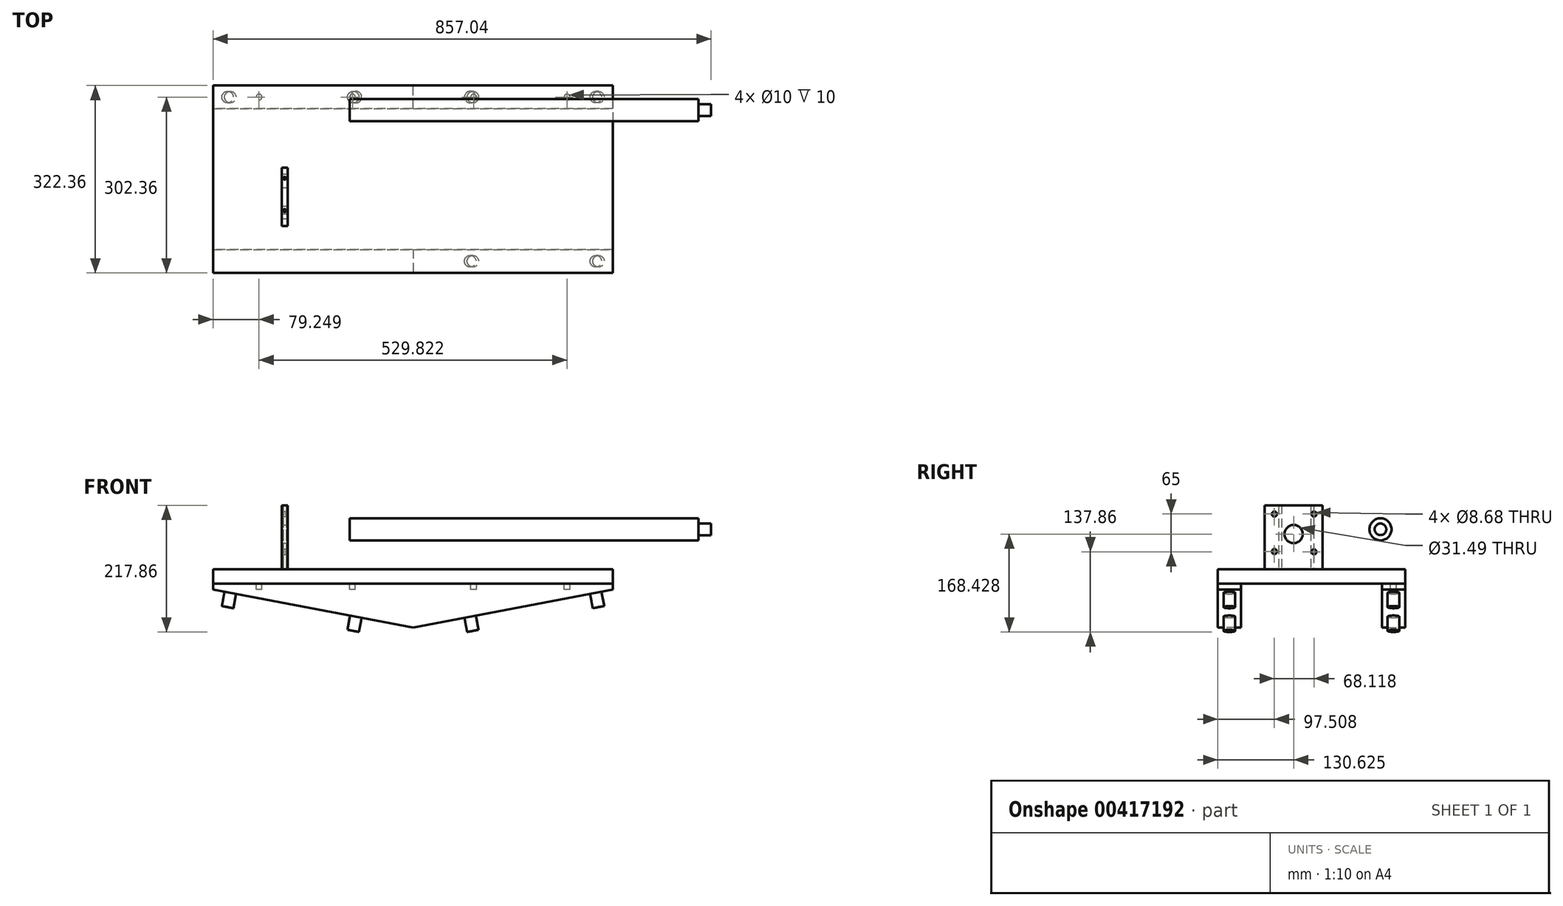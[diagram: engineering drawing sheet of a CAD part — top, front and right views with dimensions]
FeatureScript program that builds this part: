
annotation { "Feature Type Name" : "Feature", "Feature Type Description" : "" }
export const myFeature = defineFeature(function(context is Context, id is Id, definition is map)
    precondition{}
    {
        {
            var Q0;
            Q0=qCreatedBy(makeId("Front.planeOp"),FACE);
            var sketch = newSketch(context, id + "F0", { "sketchPlane" : qUnion([Q0])});
            skLineSegment(sketch, "E0", {"start": v(-343.91, 0) * mm, "end": v(-343.91, -10) * mm});
            skLineSegment(sketch, "E1", {"start": v(-343.91, -10) * mm, "end": v(0, -75) * mm});
            skLineSegment(sketch, "E2", {"start": v(0, -75) * mm, "end": v(343.91, -10) * mm});
            skLineSegment(sketch, "E3", {"start": v(343.91, -10) * mm, "end": v(343.91, 0) * mm});
            skLineSegment(sketch, "E4", {"start": v(343.91, 0) * mm, "end": v(-343.91, 0) * mm});
            skSolve(sketch);
        }
        {
            var Q0;
            Q0 = qSketchRegion(id + "F0", true);
            extrude(context, id + "F1", {"entities" : qUnion([Q0]), "depth" : 40 * mm});
        }
        {
            var Q0;
            Q0=makeQuery(id+"F1.opExtrude","SWEPT_FACE",FACE,{"disambiguationData":[OSD([sQuery(id+"F0.wireOp",EDGE,"E4")])]});
            var sketch = newSketch(context, id + "F2", { "sketchPlane" : qUnion([Q0])});
            skCircle(sketch, "E5", {"center": v(-264.91, -20) * mm, "radius": 5 * mm});
            skCircle(sketch, "E6", {"center": v(-104.19, -20) * mm, "radius": 5 * mm});
            skCircle(sketch, "E7", {"center": v(104.19, -20) * mm, "radius": 5 * mm});
            skCircle(sketch, "E8", {"center": v(264.91, -20) * mm, "radius": 5 * mm});
            skSolve(sketch);
        }
        {
            var Q0;
            Q0 = qSketchRegion(id + "F2", true);
            extrude(context, id + "F3", {"entities" : qUnion([Q0]), "operationType" : NewBodyOperationType.REMOVE, "oppositeDirection" : true, "depth" : 10 * mm});
        }
        {
            var Q0;
            Q0=makeQuery(id+"F1.opExtrude","SWEPT_FACE",FACE,{"disambiguationData":[OSD([sQuery(id+"F0.wireOp",EDGE,"E1")])]});
            var sketch = newSketch(context, id + "F4", { "sketchPlane" : qUnion([Q0])});
            skLineSegment(sketch, "E9", {"start": v(-336.07, 20) * mm, "end": v(13.93, 20) * mm, "construction": true});
            skCircle(sketch, "E10", {"center": v(-306.07, 20) * mm, "radius": 10 * mm});
            skCircle(sketch, "E11", {"center": v(-86.07, 20) * mm, "radius": 10 * mm});
            skSolve(sketch);
        }
        {
            var Q0;
            Q0 = qSketchRegion(id + "F4", true);
            extrude(context, id + "F5", {"entities" : qUnion([Q0]), "operationType" : NewBodyOperationType.ADD, "depth" : 25 * mm});
        }
        {
            var Q0;
            Q0=makeQuery(id+"F1.opExtrude","SWEPT_FACE",FACE,{"disambiguationData":[OSD([sQuery(id+"F0.wireOp",EDGE,"E2")])]});
            var sketch = newSketch(context, id + "F6", { "sketchPlane" : qUnion([Q0])});
            skCircle(sketch, "E12", {"center": v(306.07, 20) * mm, "radius": 10 * mm});
            skLineSegment(sketch, "E13", {"start": v(-13.93, 20) * mm, "end": v(336.07, 20) * mm, "construction": true});
            skCircle(sketch, "E14", {"center": v(86.07, 20) * mm, "radius": 10 * mm});
            skSolve(sketch);
        }
        {
            var Q0;
            Q0 = qSketchRegion(id + "F6", true);
            extrude(context, id + "F7", {"entities" : qUnion([Q0]), "operationType" : NewBodyOperationType.ADD, "depth" : 25 * mm});
        }
        {
            var Q0;
            Q0=qCreatedBy(makeId("Top.planeOp"),FACE);
            var sketch = newSketch(context, id + "F8", { "sketchPlane" : qUnion([Q0])});
            skLineSegment(sketch, "E15.bottom", {"start": v(343.76, 0) * mm, "end": v(-344.16, 0) * mm});
            skLineSegment(sketch, "E15.top", {"start": v(343.76, -322.36) * mm, "end": v(-344.16, -322.36) * mm});
            skLineSegment(sketch, "E15.left", {"start": v(343.76, 0) * mm, "end": v(343.76, -322.36) * mm});
            skLineSegment(sketch, "E15.right", {"start": v(-344.16, 0) * mm, "end": v(-344.16, -322.36) * mm});
            skSolve(sketch);
        }
        {
            var Q0;
            Q0 = qSketchRegion(id + "F8", true);
            extrude(context, id + "F9", {"entities" : qUnion([Q0]), "depth" : 25 * mm});
        }
        {
            var Q0;
            Q0=makeQuery(id+"F9.opExtrude","SWEPT_FACE",FACE,{"disambiguationData":[OSD([sQuery(id+"F8.wireOp",EDGE,"E15.top")])]});
            var sketch = newSketch(context, id + "F10", { "sketchPlane" : qUnion([Q0])});
            skLineSegment(sketch, "E16", {"start": v(-343.91, 0) * mm, "end": v(-343.91, -10) * mm});
            skLineSegment(sketch, "E17", {"start": v(-343.91, -10) * mm, "end": v(0, -75) * mm});
            skLineSegment(sketch, "E18", {"start": v(0, -75) * mm, "end": v(344.01, -10) * mm});
            skLineSegment(sketch, "E19", {"start": v(344.01, -10) * mm, "end": v(344.01, 0) * mm});
            skLineSegment(sketch, "E20", {"start": v(344.01, 0) * mm, "end": v(-343.91, 0) * mm});
            skSolve(sketch);
        }
        {
            var Q0;
            Q0 = qSketchRegion(id + "F10", true);
            extrude(context, id + "F11", {"entities" : qUnion([Q0]), "oppositeDirection" : true, "depth" : 40 * mm});
        }
        {
            var Q0;
            Q0=makeQuery(id+"F11.opExtrude","SWEPT_FACE",FACE,{"disambiguationData":[OSD([sQuery(id+"F10.wireOp",EDGE,"E18")])]});
            var sketch = newSketch(context, id + "F12", { "sketchPlane" : qUnion([Q0])});
            skCircle(sketch, "E21", {"center": v(306.08, 302.36) * mm, "radius": 10 * mm});
            skLineSegment(sketch, "E22", {"start": v(-13.92, 302.36) * mm, "end": v(336.08, 302.36) * mm, "construction": true});
            skCircle(sketch, "E23", {"center": v(86.08, 302.36) * mm, "radius": 10 * mm});
            skSolve(sketch);
        }
        {
            var Q0;
            Q0 = qSketchRegion(id + "F12", true);
            extrude(context, id + "F13", {"entities" : qUnion([Q0]), "operationType" : NewBodyOperationType.ADD, "depth" : 25 * mm});
        }
        {
            var Q0;
            Q0=makeQuery(id+"F9.opExtrude","CAP_FACE",FACE,{"disambiguationData":[OSD([sQuery(id+"F8.wireOp",EDGE,"E15.bottom"),sQuery(id+"F8.wireOp",EDGE,"E15.top"),sQuery(id+"F8.wireOp",EDGE,"E15.left"),sQuery(id+"F8.wireOp",EDGE,"E15.right")])],"isStart":false});
            var sketch = newSketch(context, id + "F14", { "sketchPlane" : qUnion([Q0])});
            skLineSegment(sketch, "E24.bottom", {"start": v(-225.82, -141.73) * mm, "end": v(-215.82, -141.73) * mm});
            skLineSegment(sketch, "E24.top", {"start": v(-225.82, -241.73) * mm, "end": v(-215.82, -241.73) * mm});
            skLineSegment(sketch, "E24.left", {"start": v(-225.82, -141.73) * mm, "end": v(-225.82, -241.73) * mm});
            skLineSegment(sketch, "E24.right", {"start": v(-215.82, -141.73) * mm, "end": v(-215.82, -241.73) * mm});
            skCircle(sketch, "E25", {"center": v(-220.82, -215.24) * mm, "radius": 2.5 * mm});
            skCircle(sketch, "E26", {"center": v(-220.82, -159.56) * mm, "radius": 2.5 * mm});
            skLineSegment(sketch, "E27", {"start": v(-220.82, -141.73) * mm, "end": v(-220.82, -241.73) * mm, "construction": true});
            skSolve(sketch);
        }
        {
            var Q0;
            Q0 = qSketchRegion(id + "F14", true);
            extrude(context, id + "F15", {"entities" : qUnion([Q0]), "depth" : 110 * mm});
        }
        {
            var Q0;
            Q0=makeQuery(id+"F15.opExtrude","SWEPT_FACE",FACE,{"disambiguationData":[OSD([sQuery(id+"F14.wireOp",EDGE,"E24.right")])]});
            var sketch = newSketch(context, id + "F16", { "sketchPlane" : qUnion([Q0])});
            skCircle(sketch, "E28", {"center": v(-156.73, 120) * mm, "radius": 4.34 * mm});
            skCircle(sketch, "E29", {"center": v(-156.73, 55) * mm, "radius": 4.34 * mm});
            skCircle(sketch, "E30", {"center": v(-224.85, 120) * mm, "radius": 4.34 * mm});
            skCircle(sketch, "E31", {"center": v(-224.85, 55.54) * mm, "radius": 4.34 * mm});
            skLineSegment(sketch, "E32", {"start": v(-191.73, 135) * mm, "end": v(-191.73, 25) * mm, "construction": true});
            skCircle(sketch, "E33", {"center": v(-191.73, 85.57) * mm, "radius": 15.74 * mm});
            skSolve(sketch);
        }
        {
            var Q0;
            Q0 = qSketchRegion(id + "F16", true);
            extrude(context, id + "F17", {"entities" : qUnion([Q0]), "operationType" : NewBodyOperationType.REMOVE, "oppositeDirection" : true, "depth" : 66 * mm});
        }
        {
            var Q0;
            Q0=sQuery(id+"F14.wireOp",EDGE,"E25");
            var Q1;
            Q1=sQuery(id+"F14.wireOp",EDGE,"E26");
            extrude(context, id + "F18", {"bodyType" : ToolBodyType.SURFACE, "surfaceEntities" : qUnion([Q0, Q1]), "depth" : 14.6 * mm});
        }
        {
            var Q0;
            Q0=makeQuery(id+"F15.opExtrude","SWEPT_FACE",FACE,{"disambiguationData":[OSD([sQuery(id+"F14.wireOp",EDGE,"E24.right")])]});
            cPlane(context, id + "F19", {"entities" : qUnion([Q0]), "cplaneType" : CPlaneType.OFFSET, "offset" : 107 * mm, "width" : 150 * mm, "height" : 150 * mm});
        }
        {
            var Q0;
            Q0=qCreatedBy(id+"F19.planeOp",FACE);
            var sketch = newSketch(context, id + "F20", { "sketchPlane" : qUnion([Q0])});
            skCircle(sketch, "E34", {"center": v(-42.38, 93.74) * mm, "radius": 19 * mm});
            skSolve(sketch);
        }
        {
            var Q0;
            Q0 = qSketchRegion(id + "F20", true);
            extrude(context, id + "F21", {"entities" : qUnion([Q0]), "depth" : 600 * mm});
        }
        {
            var Q0;
            Q0=makeQuery(id+"F21.opExtrude","CAP_FACE",FACE,{"disambiguationData":[OSD([sQuery(id+"F20.wireOp",EDGE,"E34")])],"isStart":false});
            var sketch = newSketch(context, id + "F22", { "sketchPlane" : qUnion([Q0])});
            skCircle(sketch, "E35", {"center": v(-42.38, 93.74) * mm, "radius": 10 * mm});
            skSolve(sketch);
        }
        {
            var Q0;
            Q0 = qSketchRegion(id + "F22", true);
            extrude(context, id + "F23", {"entities" : qUnion([Q0]), "operationType" : NewBodyOperationType.ADD, "depth" : 21.7 * mm});
        }
    });
